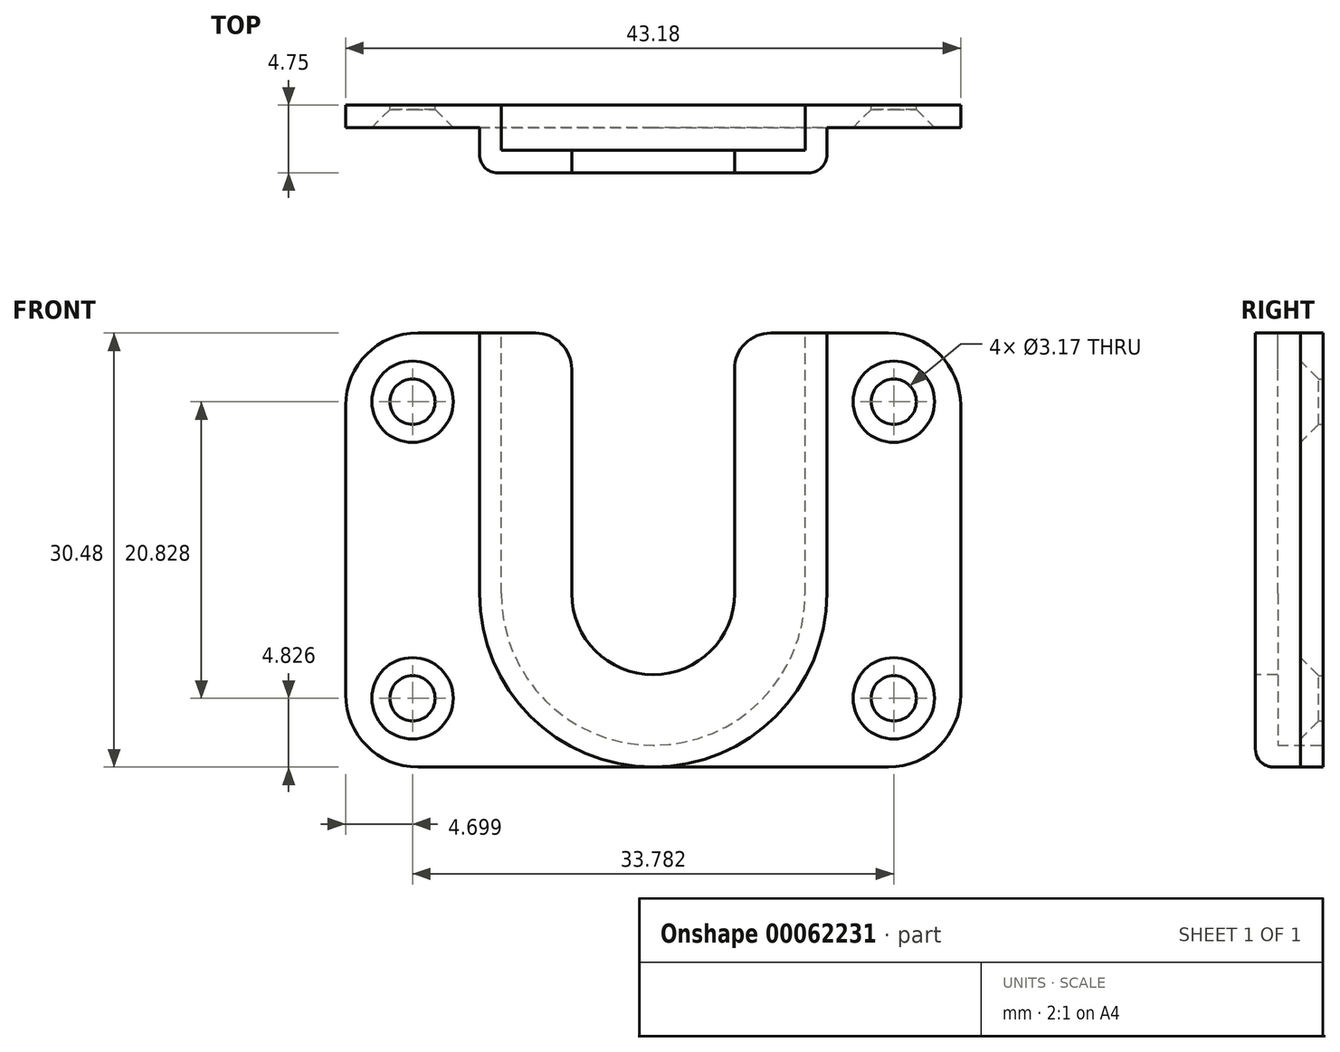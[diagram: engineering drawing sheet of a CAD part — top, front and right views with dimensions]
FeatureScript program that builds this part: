
annotation { "Feature Type Name" : "Feature", "Feature Type Description" : "" }
export const myFeature = defineFeature(function(context is Context, id is Id, definition is map)
    precondition{}
    {
        {
            var Q0;
            Q0=qCreatedBy(makeId("Front.planeOp"),FACE);
            var sketch = newSketch(context, id + "F0", { "sketchPlane" : qUnion([Q0])});
            skLineSegment(sketch, "E0.bottom", {"start": v(16.51, 15.24) * mm, "end": v(-16.5, 15.24) * mm});
            skLineSegment(sketch, "E0.top", {"start": v(16.51, -15.24) * mm, "end": v(-16.51, -15.24) * mm});
            skLineSegment(sketch, "E0.left", {"start": v(21.6, 10.16) * mm, "end": v(21.59, -10.16) * mm});
            skLineSegment(sketch, "E0.right", {"start": v(-21.59, 10.16) * mm, "end": v(-21.59, -10.16) * mm});
            skPoint(sketch, "E0.middle", {"position": v(0, 0) * mm});
            skCircle(sketch, "E1", {"center": v(16.9, 10.41) * mm, "radius": 1.59 * mm});
            skCircle(sketch, "E2.MirrorC", {"center": v(-16.9, 10.41) * mm, "radius": 1.59 * mm});
            skCircle(sketch, "E3.MirrorC", {"center": v(16.9, -10.41) * mm, "radius": 1.59 * mm});
            skCircle(sketch, "E4.MirrorC", {"center": v(-16.9, -10.41) * mm, "radius": 1.59 * mm});
            skPoint(sketch, "E5.visualSharp", {"position": v(-21.59, 15.24) * mm});
            skArc(sketch, "E5.filletArc", {"start": v(-16.5, 15.24) * mm, "mid": v(-20.1, 13.75) * mm, "end": v(-21.59, 10.16) * mm});
            skPoint(sketch, "E6.visualSharp", {"position": v(21.6, 15.24) * mm});
            skArc(sketch, "E6.filletArc", {"start": v(21.6, 10.16) * mm, "mid": v(20.1, 13.75) * mm, "end": v(16.51, 15.24) * mm});
            skPoint(sketch, "E7.visualSharp", {"position": v(21.6, -15.24) * mm});
            skArc(sketch, "E7.filletArc", {"start": v(16.51, -15.24) * mm, "mid": v(20.1, -13.75) * mm, "end": v(21.6, -10.16) * mm});
            skPoint(sketch, "E8.visualSharp", {"position": v(-21.59, -15.24) * mm});
            skArc(sketch, "E8.filletArc", {"start": v(-21.59, -10.16) * mm, "mid": v(-20.1, -13.75) * mm, "end": v(-16.51, -15.24) * mm});
            skSolve(sketch);
        }
        {
            var Q0;
            Q0=makeQuery(id+"F0.imprint","IMPRINT",FACE,{"disambiguationData":[TD([[makeQuery(id+"F0.imprint","IMPRINT",EDGE,{"derivedFrom":sQuery(id+"F0.wireOp",EDGE,"E0.bottom")}),1.0]])]});
            extrude(context, id + "F1", {"entities" : qUnion([Q0]), "depth" : 1.57 * mm});
        }
        {
            var Q0;
            Q0=makeQuery(id+"F1.opExtrude","CAP_FACE",FACE,{"disambiguationData":[OSD([sQuery(id+"F0.wireOp",EDGE,"E0.bottom"),sQuery(id+"F0.wireOp",EDGE,"E0.top"),sQuery(id+"F0.wireOp",EDGE,"E0.left"),sQuery(id+"F0.wireOp",EDGE,"E0.right"),sQuery(id+"F0.wireOp",EDGE,"E1"),sQuery(id+"F0.wireOp",EDGE,"E2.MirrorC"),sQuery(id+"F0.wireOp",EDGE,"E3.MirrorC"),sQuery(id+"F0.wireOp",EDGE,"E4.MirrorC"),sQuery(id+"F0.wireOp",EDGE,"E5.filletArc"),sQuery(id+"F0.wireOp",EDGE,"E6.filletArc"),sQuery(id+"F0.wireOp",EDGE,"E7.filletArc"),sQuery(id+"F0.wireOp",EDGE,"E8.filletArc")])],"isStart":false});
            var sketch = newSketch(context, id + "F2", { "sketchPlane" : qUnion([Q0])});
            skCircle(sketch, "E9", {"center": v(0, -3.05) * mm, "radius": 12.2 * mm});
            skLineSegment(sketch, "E10", {"start": v(12.2, 15.24) * mm, "end": v(12.2, -3.05) * mm});
            skLineSegment(sketch, "E11", {"start": v(-12.2, 15.24) * mm, "end": v(-12.2, -3.05) * mm});
            skSolve(sketch);
        }
        {
            var Q0;
            Q0 = qSketchRegion(id + "F2", true);
            var Q1;
            {var subQ0=sQuery(id+"F2.wireOp",EDGE,"E10");Q1=makeQuery(id+"F2.imprint","IMPRINT",FACE,{"disambiguationData":[TD([[makeQuery(id+"F2.imprint","IMPRINT",EDGE,{"derivedFrom":subQ0}),-1.0]])]});}
            extrude(context, id + "F3", {"entities" : qUnion([Q0, Q1]), "operationType" : NewBodyOperationType.ADD, "depth" : 3.17 * mm});
        }
        {
            var Q0;
            Q0=qCreatedBy(makeId("Front.planeOp"),FACE);
            var sketch = newSketch(context, id + "F4", { "sketchPlane" : qUnion([Q0])});
            skArc(sketch, "E12.0", {"start": v(-12.2, -3.05) * mm, "mid": v(0, -15.24) * mm, "end": v(12.2, -3.05) * mm});
            skCircle(sketch, "E13", {"center": v(0, -3.05) * mm, "radius": 10.67 * mm});
            skLineSegment(sketch, "E14.0", {"start": v(16.51, 15.24) * mm, "end": v(-16.5, 15.24) * mm});
            skLineSegment(sketch, "E15", {"start": v(10.67, -3.05) * mm, "end": v(10.67, 15.24) * mm});
            skLineSegment(sketch, "E16", {"start": v(-10.67, -3.05) * mm, "end": v(-10.67, 15.24) * mm});
            skSolve(sketch);
        }
        {
            var Q0;
            Q0 = qSketchRegion(id + "F4", true);
            extrude(context, id + "F5", {"entities" : qUnion([Q0]), "operationType" : NewBodyOperationType.REMOVE, "depth" : 3.17 * mm});
        }
        {
            var Q0;
            Q0=makeQuery(id+"F3.opExtrude","CAP_FACE",FACE,{"disambiguationData":[OSD([sQuery(id+"F0.wireOp",EDGE,"E0.bottom"),sQuery(id+"F2.wireOp",EDGE,"E9"),sQuery(id+"F2.wireOp",EDGE,"E10"),sQuery(id+"F2.wireOp",EDGE,"E11")])],"isStart":false});
            var sketch = newSketch(context, id + "F6", { "sketchPlane" : qUnion([Q0])});
            skArc(sketch, "E17.0", {"start": v(-12.2, -3.05) * mm, "mid": v(0, -15.24) * mm, "end": v(12.2, -3.05) * mm});
            skLineSegment(sketch, "E18.0", {"start": v(12.2, 15.24) * mm, "end": v(-12.2, 15.24) * mm});
            skCircle(sketch, "E19", {"center": v(0, -3.05) * mm, "radius": 5.72 * mm});
            skLineSegment(sketch, "E20", {"start": v(5.72, -3.05) * mm, "end": v(5.71, 15.24) * mm});
            skLineSegment(sketch, "E21", {"start": v(-5.72, -3.05) * mm, "end": v(-5.72, 15.24) * mm});
            skSolve(sketch);
        }
        {
            var Q0;
            Q0 = qSketchRegion(id + "F6", true);
            extrude(context, id + "F7", {"entities" : qUnion([Q0]), "operationType" : NewBodyOperationType.REMOVE, "endBound" : BoundingType.THROUGH_ALL, "oppositeDirection" : true, "depth" : 25.4 * mm});
        }
        {
            var Q0;
            Q0=makeQuery(id+"F3.opExtrude","CAP_FACE",FACE,{"disambiguationData":[OSD([sQuery(id+"F0.wireOp",EDGE,"E0.bottom"),sQuery(id+"F2.wireOp",EDGE,"E9"),sQuery(id+"F2.wireOp",EDGE,"E10"),sQuery(id+"F2.wireOp",EDGE,"E11")])],"isStart":false});
            var sketch = newSketch(context, id + "F8", { "sketchPlane" : qUnion([Q0])});
            skLineSegment(sketch, "E22.0", {"start": v(-8.26, 15.24) * mm, "end": v(-12.2, 15.24) * mm});
            skLineSegment(sketch, "E23.0", {"start": v(-5.72, -3.05) * mm, "end": v(-5.72, 12.7) * mm});
            skLineSegment(sketch, "E24.0", {"start": v(5.72, -3.05) * mm, "end": v(5.71, 12.7) * mm});
            skLineSegment(sketch, "E25.0", {"start": v(12.2, 15.24) * mm, "end": v(8.26, 15.24) * mm});
            skPoint(sketch, "E26.visualSharp", {"position": v(-5.72, 15.24) * mm});
            skArc(sketch, "E26.filletArc", {"start": v(-5.72, 12.7) * mm, "mid": v(-6.46, 14.5) * mm, "end": v(-8.26, 15.24) * mm});
            skPoint(sketch, "E27.visualSharp", {"position": v(5.71, 15.24) * mm});
            skArc(sketch, "E27.filletArc", {"start": v(8.26, 15.24) * mm, "mid": v(6.46, 14.5) * mm, "end": v(5.72, 12.7) * mm});
            skSolve(sketch);
        }
        {
            var Q0;
            Q0 = qSketchRegion(id + "F8", true);
            var Q1;
            {var subQ0=sQuery(id+"F8.wireOp",EDGE,"E26.filletArc");Q1=makeQuery(id+"F8.imprint","IMPRINT",FACE,{"disambiguationData":[TD([[makeQuery(id+"F8.imprint","IMPRINT",EDGE,{"derivedFrom":subQ0}),-1.0]])]});}
            var Q2;
            {var subQ0=sQuery(id+"F8.wireOp",EDGE,"E27.filletArc");Q2=makeQuery(id+"F8.imprint","IMPRINT",FACE,{"disambiguationData":[TD([[makeQuery(id+"F8.imprint","IMPRINT",EDGE,{"derivedFrom":subQ0}),-1.0]])]});}
            extrude(context, id + "F9", {"entities" : qUnion([Q0, Q1, Q2]), "operationType" : NewBodyOperationType.REMOVE, "endBound" : BoundingType.THROUGH_ALL, "oppositeDirection" : true, "depth" : 25.4 * mm});
        }
        {
            var Q0;
            Q0=makeQuery(id+"F3.opExtrude","CAP_EDGE",EDGE,{"disambiguationData":[OSD([sQuery(id+"F2.wireOp",EDGE,"E9")])],"isStart":false});
            var Q1;
            Q1=makeQuery(id+"F3.opExtrude","CAP_EDGE",EDGE,{"disambiguationData":[OSD([sQuery(id+"F2.wireOp",EDGE,"E11")])],"isStart":false});
            var Q2;
            Q2=makeQuery(id+"F3.opExtrude","CAP_EDGE",EDGE,{"disambiguationData":[OSD([sQuery(id+"F2.wireOp",EDGE,"E10")])],"isStart":false});
            fillet(context, id + "F10", {"entities" : qUnion([Q0, Q1, Q2]), "radius" : 1.27 * mm, "tangentPropagation" : true, "allowEdgeOverflow" : false});
        }
        {
            var Q0;
            Q0=makeQuery(id+"F1.opExtrude","CAP_EDGE",EDGE,{"disambiguationData":[OSD([sQuery(id+"F0.wireOp",EDGE,"E2.MirrorC")])],"isStart":false});
            var Q1;
            Q1=makeQuery(id+"F1.opExtrude","CAP_EDGE",EDGE,{"disambiguationData":[OSD([sQuery(id+"F0.wireOp",EDGE,"E4.MirrorC")])],"isStart":false});
            var Q2;
            Q2=makeQuery(id+"F1.opExtrude","CAP_EDGE",EDGE,{"disambiguationData":[OSD([sQuery(id+"F0.wireOp",EDGE,"E1")])],"isStart":false});
            var Q3;
            Q3=makeQuery(id+"F1.opExtrude","CAP_EDGE",EDGE,{"disambiguationData":[OSD([sQuery(id+"F0.wireOp",EDGE,"E3.MirrorC")])],"isStart":false});
            chamfer(context, id + "F11", {"entities" : qUnion([Q0, Q1, Q2, Q3]), "width" : 1.27 * mm, "tangentPropagation" : true});
        }
    });
